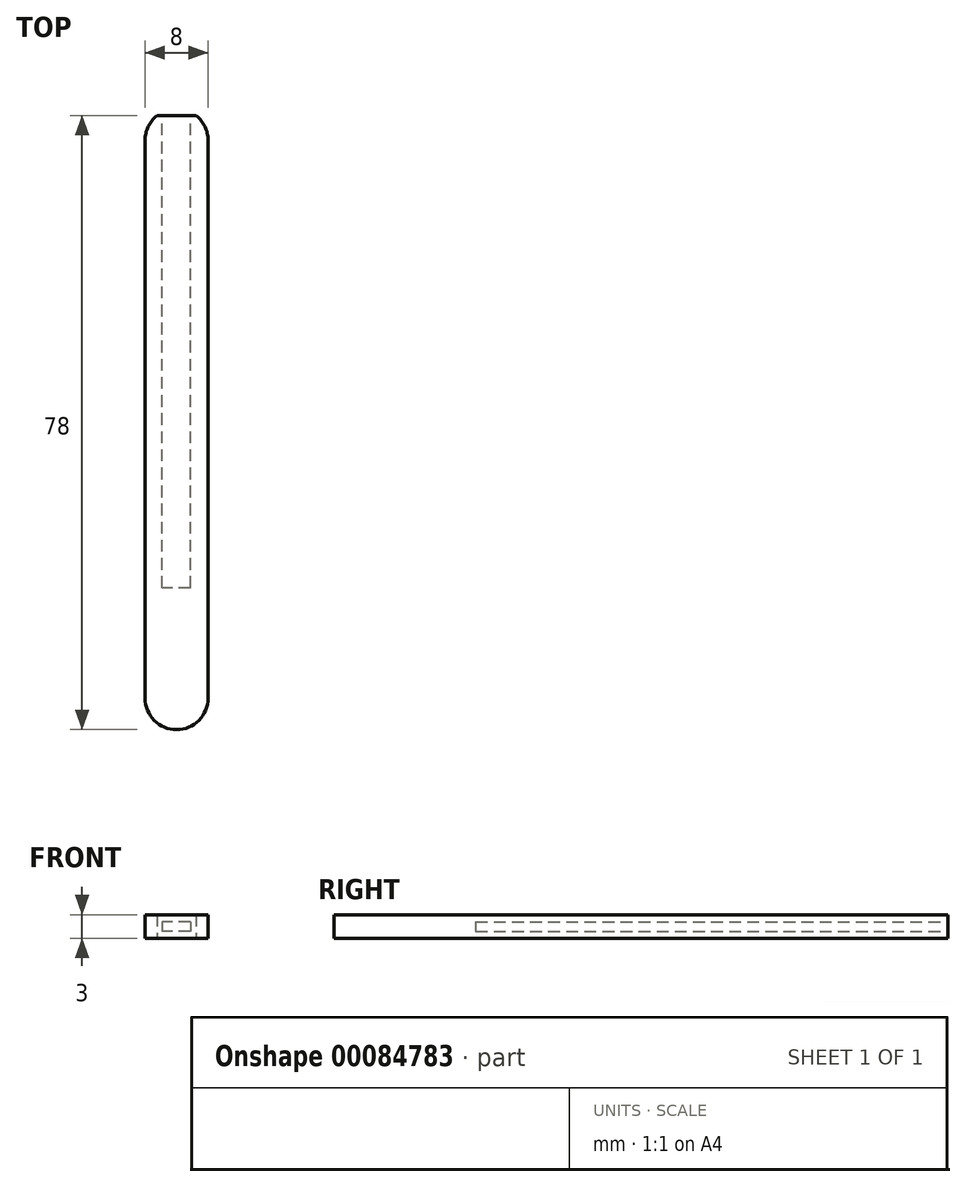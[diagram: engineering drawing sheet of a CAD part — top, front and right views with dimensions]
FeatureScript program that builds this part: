
annotation { "Feature Type Name" : "Feature", "Feature Type Description" : "" }
export const myFeature = defineFeature(function(context is Context, id is Id, definition is map)
    precondition{}
    {
        {
            var Q0;
            Q0=qCreatedBy(makeId("Top.planeOp"),FACE);
            var sketch = newSketch(context, id + "F0", { "sketchPlane" : qUnion([Q0])});
            skArc(sketch, "E0", {"start": v(4.02, 0) * mm, "mid": v(3.63, 1.73) * mm, "end": v(2.52, 3.12) * mm});
            skLineSegment(sketch, "E1", {"start": v(-3.98, 0) * mm, "end": v(-3.98, -70.88) * mm});
            skArc(sketch, "E2", {"start": v(-3.98, -70.88) * mm, "mid": v(0.02, -74.88) * mm, "end": v(4.02, -70.88) * mm});
            skLineSegment(sketch, "E3", {"start": v(4.02, 0) * mm, "end": v(4.02, -70.88) * mm});
            skLineSegment(sketch, "E4", {"start": v(-2.48, 3.12) * mm, "end": v(2.52, 3.12) * mm});
            skArc(sketch, "E5.trimOffspring", {"start": v(-2.48, 3.12) * mm, "mid": v(-3.58, 1.73) * mm, "end": v(-3.98, 0) * mm});
            skPoint(sketch, "E6", {"position": v(0, -74.88) * mm});
            skSolve(sketch);
        }
        {
            var Q0;
            Q0=makeQuery(id+"F0.imprint","IMPRINT",FACE,{"disambiguationData":[TD([[makeQuery(id+"F0.imprint","IMPRINT",EDGE,{"derivedFrom":sQuery(id+"F0.wireOp",EDGE,"E0")}),1.0]])]});
            extrude(context, id + "F1", {"entities" : qUnion([Q0]), "depth" : 3 * mm});
        }
        {
            var Q0;
            Q0=makeQuery(id+"F1.opExtrude","SWEPT_FACE",FACE,{"disambiguationData":[OSD([sQuery(id+"F0.wireOp",EDGE,"E4")])]});
            var sketch = newSketch(context, id + "F2", { "sketchPlane" : qUnion([Q0])});
            skLineSegment(sketch, "E7.bottom", {"start": v(-1.8, 2.1) * mm, "end": v(1.8, 2.1) * mm});
            skLineSegment(sketch, "E7.top", {"start": v(-1.8, 0.9) * mm, "end": v(1.8, 0.9) * mm});
            skLineSegment(sketch, "E7.left", {"start": v(-1.8, 2.1) * mm, "end": v(-1.8, 0.9) * mm});
            skLineSegment(sketch, "E7.right", {"start": v(1.8, 2.1) * mm, "end": v(1.8, 0.9) * mm});
            skLineSegment(sketch, "E8", {"start": v(-1.8, 1.5) * mm, "end": v(-2.52, 1.5) * mm, "construction": true});
            skLineSegment(sketch, "E9", {"start": v(0, 2.1) * mm, "end": v(0, 3) * mm, "construction": true});
            skSolve(sketch);
        }
        {
            var Q0;
            Q0=qSketchRegion(id+"F2",true);
            extrude(context, id + "F3", {"entities" : qUnion([Q0]), "operationType" : NewBodyOperationType.REMOVE, "oppositeDirection" : true, "depth" : 60 * mm});
        }
    });
